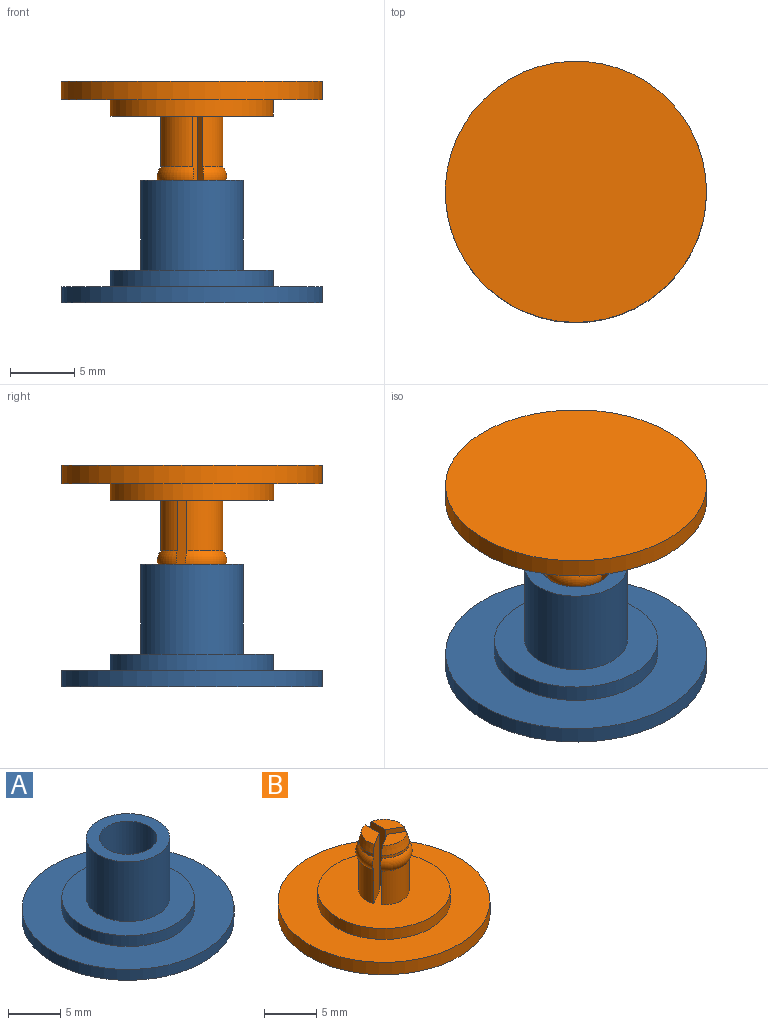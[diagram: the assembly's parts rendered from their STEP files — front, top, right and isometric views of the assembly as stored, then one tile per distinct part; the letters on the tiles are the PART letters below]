
ASSEMBLY  parts=2 mates=1
PART A: 11 faces, bbox 20.3x20.3x9.5 mm
  f0: plane 12.7x12.7mm, normal (0,0,1), area 76.4mm2, adj f1,f7
  f1: cylinder r=4mm len=8mm, axis (0,0,1), area 175.9mm2, adj f0,f2
  f2: plane 8x8mm, normal (0,0,1), area 26.5mm2, adj f1,f3
  f3: cylinder r=2.75mm len=5.5mm, axis (0,0,1), area 68.7mm2, adj f2,f4
  f4: torus R=2.29mm, axis (0,0,1), area 34.9mm2, adj f3,f5
  f5: cylinder r=2.75mm len=5.5mm, axis (0,0,1), area 25.9mm2, adj f4,f6
  f6: plane 5.5x5.5mm, normal (0,0,1), area 23.8mm2, adj f5
  f7: cylinder r=6.35mm len=12.7mm, axis (0,0,1), area 50.7mm2, adj f0,f8
  f8: plane 20.32x20.32mm, normal (0,0,1), area 197.6mm2, adj f7,f10
  f9: plane 20.32x20.32mm, normal (0,0,-1), area 324.3mm2, adj f10
  f10: cylinder r=10.16mm len=20.32mm, axis (0,0,1), area 81.1mm2, adj f8,f9
PART B: 26 faces, bbox 20.3x20.3x9.5 mm
  f0: cylinder r=2.41mm len=3.96mm, axis (0,0,-1), area 16.9mm2, adj f3,f14,f20,f21
  f1: cylinder r=2.41mm len=3.96mm, axis (0,0,-1), area 16.9mm2, adj f4,f14,f22,f23
  f2: cylinder r=2.41mm len=3.96mm, axis (0,0,-1), area 16.9mm2, adj f5,f14,f24,f25
  f3: torus R=1.56mm, axis (0,0,-1), area 7.8mm2, adj f0,f6,f20,f21
  f4: torus R=1.56mm, axis (0,0,-1), area 7.8mm2, adj f1,f7,f22,f23
  f5: torus R=1.56mm, axis (0,0,-1), area 7.8mm2, adj f2,f8,f24,f25
  f6: cylinder r=2.41mm len=3.23mm, axis (0,0,-1), area 1.3mm2, adj f3,f11,f20,f21
  f7: cylinder r=2.41mm len=3.73mm, axis (0,0,-1), area 1.3mm2, adj f4,f12,f22,f23
  f8: cylinder r=2.41mm len=3.23mm, axis (0,0,-1), area 1.3mm2, adj f5,f13,f24,f25
  f9: plane 2.85x1.77mm, normal (0,0,1), area 3.3mm2, adj f11,f20,f21
  f10: plane 3.29x1.7mm, normal (0,0,1), area 3.3mm2, adj f12,f22,f23
  f11: cone r=2.41mm half-angle=14deg, axis (0,0,-1), area 4.1mm2, adj f6,f9,f20,f21
  f12: cone r=2.41mm half-angle=14deg, axis (0,0,-1), area 4.1mm2, adj f7,f10,f22,f23
  f13: cone r=2.41mm half-angle=14deg, axis (0,0,-1), area 4.1mm2, adj f8,f15,f24,f25
  f14: plane 12.7x12.7mm, normal (0,0,1), area 113.8mm2, adj f0,f1,f2,f16,f20,f21,f22,f23
  f15: plane 2.85x1.77mm, normal (0,0,1), area 3.3mm2, adj f13,f24,f25
  f16: cylinder r=6.35mm len=12.7mm, axis (0,0,1), area 50.7mm2, adj f14,f17
  f17: plane 20.32x20.32mm, normal (0,0,1), area 197.6mm2, adj f16,f19
  f18: plane 20.32x20.32mm, normal (0,0,-1), area 324.3mm2, adj f19
  f19: cylinder r=10.16mm len=20.32mm, axis (0,0,-1), area 92.9mm2, adj f17,f18
  f20: plane 6.8x2.45mm, normal (1,0,0), area 14.8mm2, adj f0,f3,f6,f9,f11,f14,f21
  f21: plane 6.8x2.12mm, normal (0.5,-0.87,0), area 14.8mm2, adj f0,f3,f6,f9,f11,f14,f20
  f22: plane 6.8x2.12mm, normal (-0.5,0.87,0), area 14.8mm2, adj f1,f4,f7,f10,f12,f14,f23
  f23: plane 6.8x2.12mm, normal (0.5,0.87,0), area 14.8mm2, adj f1,f4,f7,f10,f12,f14,f22
  f24: plane 6.8x2.45mm, normal (-1,0,0), area 14.8mm2, adj f2,f5,f8,f13,f14,f15,f25
  f25: plane 6.8x2.12mm, normal (-0.5,-0.87,0), area 14.8mm2, adj f2,f5,f8,f13,f14,f15,f24
PLACE A t=(-2.4,1.86,0.87)mm fixed
PLACE B rot(axis=(-0.41,-0.91,0),180deg) t=(-2.4,1.86,18.14)mm
MATE cylindrical B.f0 <-> A.f1  axis (0,0,1) through (-2.4,1.86,13.43)mm
